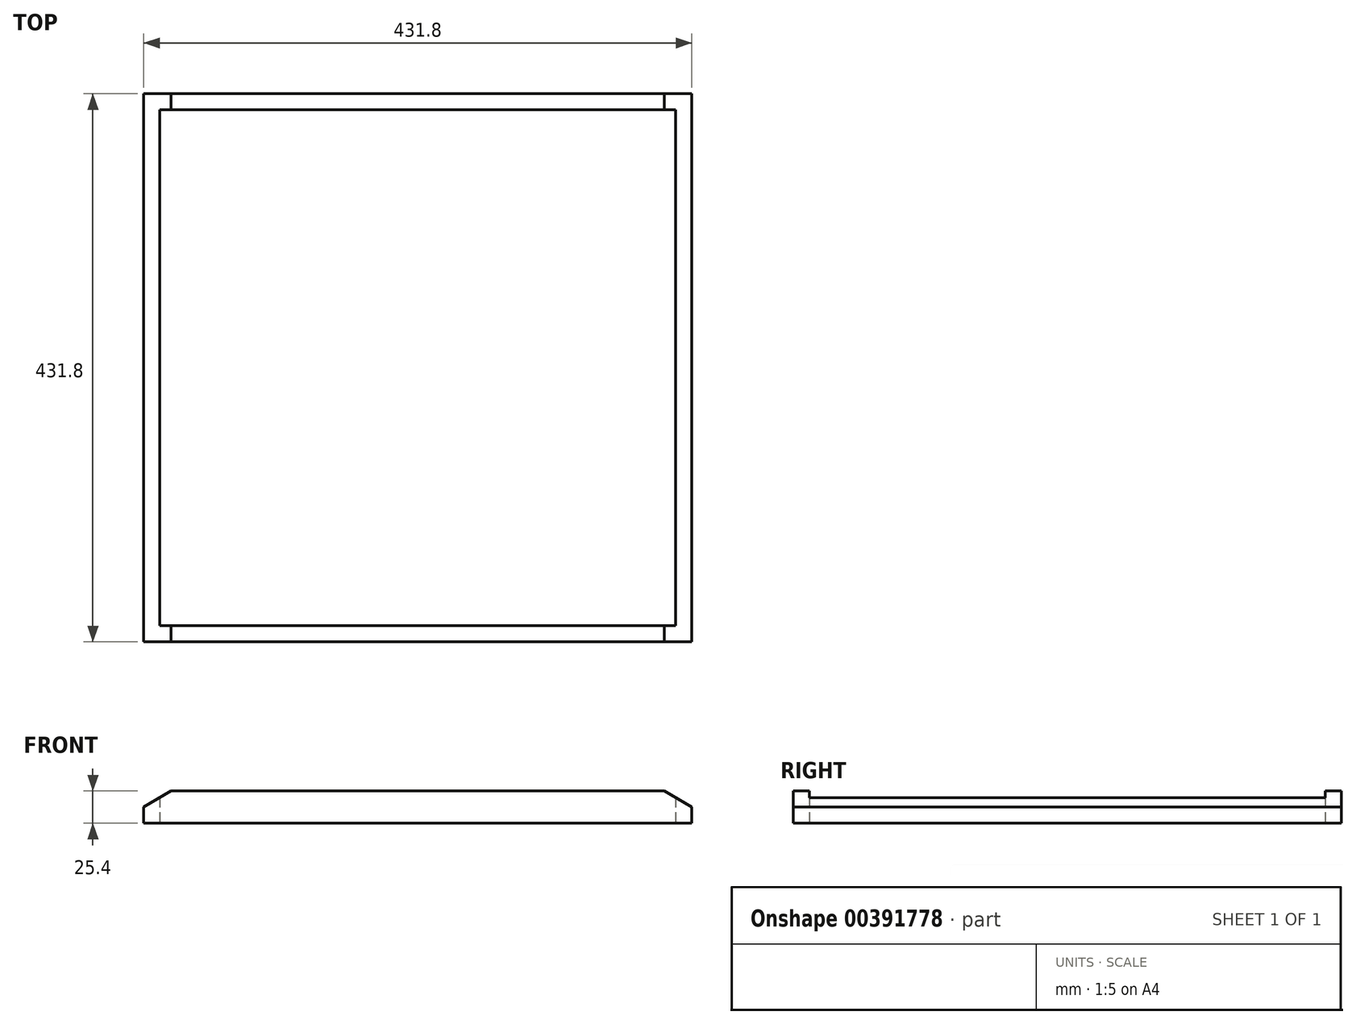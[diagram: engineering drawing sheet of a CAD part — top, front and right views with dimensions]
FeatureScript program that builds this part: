
annotation { "Feature Type Name" : "Feature", "Feature Type Description" : "" }
export const myFeature = defineFeature(function(context is Context, id is Id, definition is map)
    precondition{}
    {
        {
            var Q0;
            Q0=qCreatedBy(makeId("Top.planeOp"),FACE);
            var sketch = newSketch(context, id + "F0", { "sketchPlane" : qUnion([Q0])});
            skLineSegment(sketch, "E0.bottom", {"start": v(-203.2, 203.2) * mm, "end": v(203.2, 203.2) * mm});
            skLineSegment(sketch, "E0.top", {"start": v(-203.2, -203.2) * mm, "end": v(203.2, -203.2) * mm});
            skLineSegment(sketch, "E0.left", {"start": v(-203.2, 203.2) * mm, "end": v(-203.2, -203.2) * mm});
            skLineSegment(sketch, "E0.right", {"start": v(203.2, 203.2) * mm, "end": v(203.2, -203.2) * mm});
            skPoint(sketch, "E0.middle", {"position": v(0, 0) * mm});
            skLineSegment(sketch, "E1.bottom", {"start": v(-215.9, 215.9) * mm, "end": v(215.9, 215.9) * mm});
            skLineSegment(sketch, "E1.top", {"start": v(-215.9, -215.9) * mm, "end": v(215.9, -215.9) * mm});
            skLineSegment(sketch, "E1.left", {"start": v(-215.9, 215.9) * mm, "end": v(-215.9, -215.9) * mm});
            skLineSegment(sketch, "E1.right", {"start": v(215.9, 215.9) * mm, "end": v(215.9, -215.9) * mm});
            skSolve(sketch);
        }
        {
            var Q0;
            Q0=makeQuery(id+"F0.imprint","IMPRINT",FACE,{"disambiguationData":[TD([[makeQuery(id+"F0.imprint","IMPRINT",EDGE,{"derivedFrom":sQuery(id+"F0.wireOp",EDGE,"E0.bottom")}),1.0]])]});
            extrude(context, id + "F1", {"entities" : qUnion([Q0]), "depth" : 25.4 * mm});
        }
        {
            var Q0;
            Q0=makeQuery(id+"F1.opExtrude","SWEPT_FACE",FACE,{"disambiguationData":[OSD([sQuery(id+"F0.wireOp",EDGE,"E1.top")])]});
            var sketch = newSketch(context, id + "F2", { "sketchPlane" : qUnion([Q0])});
            skLineSegment(sketch, "E2", {"start": v(-215.9, 12.7) * mm, "end": v(-194.25, 25.4) * mm});
            skLineSegment(sketch, "E3.MirrorCS", {"start": v(215.9, 12.7) * mm, "end": v(194.25, 25.4) * mm});
            skSolve(sketch);
        }
        {
            var Q0;
            {var subQ0=sQuery(id+"F2.wireOp",EDGE,"E2");Q0=makeQuery(id+"F2.imprint","IMPRINT",FACE,{"disambiguationData":[TD([[makeQuery(id+"F2.imprint","IMPRINT",EDGE,{"derivedFrom":subQ0}),1.0]])]});}
            var Q1;
            {var subQ0=sQuery(id+"F2.wireOp",EDGE,"E3.MirrorCS");Q1=makeQuery(id+"F2.imprint","IMPRINT",FACE,{"disambiguationData":[TD([[makeQuery(id+"F2.imprint","IMPRINT",EDGE,{"derivedFrom":subQ0}),-1.0]])]});}
            extrude(context, id + "F3", {"entities" : qUnion([Q0, Q1]), "operationType" : NewBodyOperationType.REMOVE, "oppositeDirection" : true, "depth" : 431.8 * mm});
        }
    });
